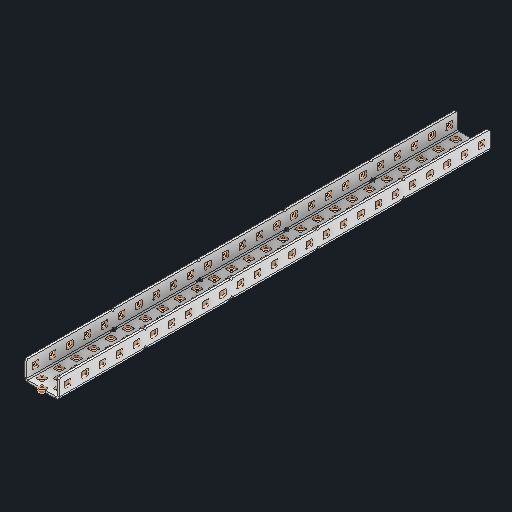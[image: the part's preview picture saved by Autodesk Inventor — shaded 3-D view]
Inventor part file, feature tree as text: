
AUTODESK INVENTOR PART (.ipt)
format: ipt  version: 2025 (Build 290162000, 162)  size: 2,050,048 bytes
history: native  units: in
note: dims shown in document units (in); Inventor stores cm internally (conversion verified against a paired STEP export)
features: other x256, sketch x5, sheet_metal_op x1
ambient origin geometry x8: Origin, YZ Plane, XZ Plane, XY Plane, X Axis, Y Axis, Z Axis, Center Point
bodies: Solid1 (feature_tree)
feature tree (262):
  other  "Alu C 1x2x1x25.ipt"
  other  "Solid1::Alu C 1x2x1x25.ipt"
  other  "TaggingFeature1"
  sketch  "Sketch1"  dims[d0=0.3937in]
  sketch  "Sketch2"  dims[d1=0.0625in]
  sketch  "Sketch3"
  other  "Flange Pattern Sketch"
  sketch  "Sketch9"
  sheet_metal_op  "Body Pattern Sketch"
  other  "Arc Length"
  sketch  "Sketch14"
  other  "Flange Pattern Plane"
  other  "Srf1"
  other  "Srf2"
  other  "Srf3"
  other  "Srf4"
  other  "Srf5"
  other  "Srf6"
  other  "Srf7"
  other  "Srf8"
  other  "Srf9"
  other  "Srf10"
  other  "Srf11"
  other  "Srf12"
  other  "Srf13"
  other  "Srf14"
  other  "Srf15"
  other  "Srf16"
  other  "Srf17"
  other  "Srf18"
  other  "Srf19"
  other  "Srf20"
  other  "Srf21"
  other  "Srf22"
  other  "Srf23"
  other  "Srf24"
  other  "Srf25"
  other  "Srf26"
  other  "Srf27"
  other  "Srf28"
  other  "Srf29"
  other  "Srf30"
  other  "Srf31"
  other  "Srf32"
  other  "Srf33"
  other  "Srf34"
  other  "Srf35"
  other  "Srf36"
  other  "Srf37"
  other  "Srf38"
  other  "Srf39"
  other  "Srf40"
  other  "Srf41"
  other  "Srf42"
  other  "Srf43"
  other  "Srf44"
  other  "Srf45"
  other  "Srf46"
  other  "Srf47"
  other  "Srf48"
  other  "Srf49"
  other  "Srf50"
  other  "Srf51"
  other  "Srf52"
  other  "Srf53"
  other  "Srf54"
  other  "Srf55"
  other  "Srf56"
  other  "Srf57"
  other  "Srf58"
  other  "Srf59"
  other  "Srf60"
  other  "Srf61"
  other  "Srf62"
  other  "Srf63"
  other  "Srf64"
  other  "Srf65"
  other  "Srf66"
  other  "Srf67"
  other  "Srf68"
  other  "Srf69"
  other  "Srf70"
  other  "Srf71"
  other  "Srf72"
  other  "Srf73"
  other  "Srf74"
  other  "Srf75"
  other  "Srf76"
  other  "Srf77"
  other  "Srf78"
  other  "Srf79"
  other  "Srf80"
  other  "Srf81"
  other  "Srf82"
  other  "Srf83"
  other  "Srf84"
  other  "Srf85"
  other  "Srf86"
  other  "Srf87"
  other  "Srf88"
  other  "Srf89"
  other  "Srf90"
  other  "Srf91"
  other  "Srf92"
  other  "Srf93"
  other  "Srf94"
  other  "Srf95"
  other  "Srf96"
  other  "Srf97"
  other  "Srf98"
  other  "Srf99"
  other  "Srf100"
  other  "Srf101"
  other  "Srf102"
  other  "Srf103"
  other  "Srf104"
  other  "Srf105"
  other  "Srf106"
  other  "Srf107"
  other  "Srf108"
  other  "Srf109"
  other  "Srf110"
  other  "Srf111"
  other  "Srf112"
  other  "Srf113"
  other  "Srf114"
  other  "Srf115"
  other  "Srf116"
  other  "Srf117"
  other  "Srf118"
  other  "Srf119"
  other  "Srf120"
  other  "Srf121"
  other  "Srf122"
  other  "Srf123"
  other  "Srf124"
  other  "Srf125"
  other  "Srf1::Derived"
  other  "Srf2::Derived"
  other  "Srf823::Derived"
  other  "Srf824::Derived"
  other  "Srf825::Derived"
  other  "Srf826::Derived"
  other  "Srf827::Derived"
  other  "Srf828::Derived"
  other  "Srf829::Derived"
  other  "Srf922::Derived"
  other  "Srf923::Derived"
  other  "Srf924::Derived"
  other  "Srf925::Derived"
  other  "Srf926::Derived"
  other  "Srf1143::Derived"
  other  "Srf1144::Derived"
  other  "Srf1145::Derived"
  other  "Srf1146::Derived"
  other  "Srf1147::Derived"
  other  "Srf1148::Derived"
  other  "Srf1149::Derived"
  other  "Srf1150::Derived"
  other  "Srf1151::Derived"
  other  "Srf1152::Derived"
  other  "Srf1153::Derived"
  other  "Srf1154::Derived"
  other  "Srf1155::Derived"
  other  "Srf1156::Derived"
  other  "Srf1157::Derived"
  other  "Srf1158::Derived"
  other  "Srf1159::Derived"
  other  "Srf1160::Derived"
  other  "Srf1161::Derived"
  other  "Srf1162::Derived"
  other  "Srf1163::Derived"
  other  "Srf1164::Derived"
  other  "Srf1165::Derived"
  other  "Srf1166::Derived"
  other  "Srf1167::Derived"
  other  "Srf1168::Derived"
  other  "Srf1169::Derived"
  other  "Srf1170::Derived"
  other  "Srf1171::Derived"
  other  "Srf1172::Derived"
  other  "Srf1173::Derived"
  other  "Srf1174::Derived"
  other  "Srf1175::Derived"
  other  "Srf1176::Derived"
  other  "Srf1177::Derived"
  other  "Srf1178::Derived"
  other  "Srf91::Derived"
  other  "Srf92::Derived"
  other  "Srf856::Derived"
  other  "Srf857::Derived"
  other  "Srf858::Derived"
  other  "Srf859::Derived"
  other  "Srf860::Derived"
  other  "Srf861::Derived"
  other  "Srf862::Derived"
  other  "Srf959::Derived"
  other  "Srf960::Derived"
  other  "Srf961::Derived"
  other  "Srf962::Derived"
  other  "Srf963::Derived"
  other  "Srf1199::Derived"
  other  "Srf1200::Derived"
  other  "Srf1201::Derived"
  other  "Srf1202::Derived"
  other  "Srf1203::Derived"
  other  "Srf1204::Derived"
  other  "Srf1205::Derived"
  other  "Srf1206::Derived"
  other  "Srf1207::Derived"
  other  "Srf1208::Derived"
  other  "Srf1209::Derived"
  other  "Srf1210::Derived"
  other  "Srf1211::Derived"
  other  "Srf1212::Derived"
  other  "Srf1213::Derived"
  other  "Srf1214::Derived"
  other  "Srf1215::Derived"
  other  "Srf1216::Derived"
  other  "Srf1217::Derived"
  other  "Srf1218::Derived"
  other  "Srf1219::Derived"
  other  "Srf1220::Derived"
  other  "Srf1221::Derived"
  other  "Srf1222::Derived"
  other  "Srf1223::Derived"
  other  "Srf1224::Derived"
  other  "Srf1225::Derived"
  other  "Srf1226::Derived"
  other  "Srf1227::Derived"
  other  "Srf1228::Derived"
  other  "Srf1229::Derived"
  other  "Srf1230::Derived"
  other  "Srf1231::Derived"
  other  "Srf1232::Derived"
  other  "Srf1233::Derived"
  other  "Srf1234::Derived"
  other  "Srf786::Derived"
  other  "Srf889::Derived"
  other  "Srf890::Derived"
  other  "Srf891::Derived"
  other  "Srf892::Derived"
  other  "Srf893::Derived"
  other  "Srf894::Derived"
  other  "Srf895::Derived"
  other  "Srf896::Derived"
  other  "Srf996::Derived"
  other  "Srf997::Derived"
  other  "Srf998::Derived"
  other  "Srf999::Derived"
  other  "Srf1000::Derived"
  other  "Srf1255::Derived"
  other  "Srf1256::Derived"
  other  "Srf1257::Derived"
  other  "Srf1258::Derived"
  other  "Srf1259::Derived"
  other  "Srf1260::Derived"
  other  "Srf1261::Derived"
  other  "Srf1262::Derived"
  other  "Srf1263::Derived"
  other  "Srf1264::Derived"
  other  "Srf1265::Derived"
